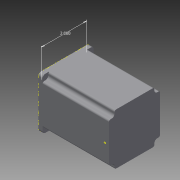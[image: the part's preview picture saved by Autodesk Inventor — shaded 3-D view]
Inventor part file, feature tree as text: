
AUTODESK INVENTOR PART (.ipt)
format: ipt  version: 2013 (Build 170138000, 138)  size: 177,664 bytes
history: native  units: in
note: dims shown in document units (in); Inventor stores cm internally (conversion verified against a paired STEP export)
features: sketch x6, extrude x5, other x1, fillet x1
ambient origin geometry x8: Origin, YZ Plane, XZ Plane, XY Plane, X Axis, Y Axis, Z Axis, Center Point
bodies: Solid1 (feature_tree)
feature tree (13):
  extrude  "Extrusion1"  Depth=2.25in
  extrude  "Extrusion2"  Depth=1.5in
  extrude  "Extrusion3"  Depth=0.25in
  extrude  "Extrusion4"  Depth=0.23in
  other  "motorLead"
  extrude  "Extrusion6"  Depth=0.125in
  fillet  "Fillet1"  Radius=1.125in
  sketch  "Sketch6"  dims[d19=1.125in d22=0.25in d24=0.25in d25=0.25in d26=0.25in d27=0.25in d28=0.25in d29=0.25in d30=0.25in d31=0.25in d32=0.25in d33=2.915in d34=0.0in d35=0.075in d36=2.0in]
  sketch  "Sketch1"  dims[d0=2.25in d1=2.25in]
  sketch  "Sketch2"  dims[d2=3.1in d3=0.0in d4=1.5in]
  sketch  "Sketch3"  dims[d8=0.06in d9=0.0in d10=0.25in]
  sketch  "Sketch4"  dims[d11=0.75in d12=0.0in d13=0.23in]
  sketch  "Sketch5"  dims[d15=0.59in d16=0.0in d17=0.125in d18=1.125in]
